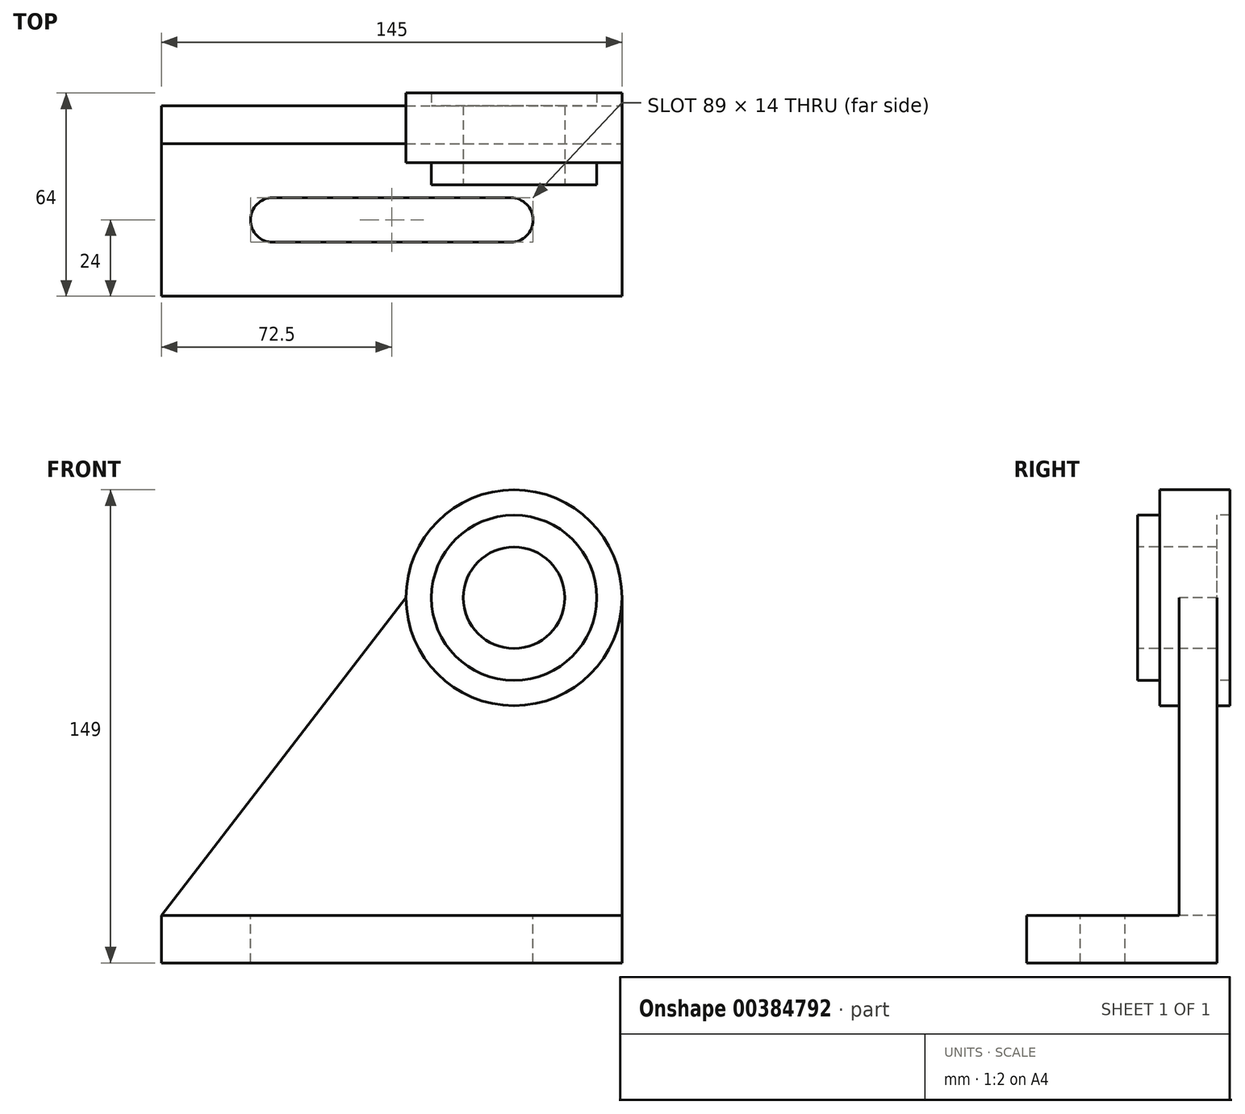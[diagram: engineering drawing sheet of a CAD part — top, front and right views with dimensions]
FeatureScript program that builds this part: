
annotation { "Feature Type Name" : "Feature", "Feature Type Description" : "" }
export const myFeature = defineFeature(function(context is Context, id is Id, definition is map)
    precondition{}
    {
        {
            var Q0;
            Q0=qCreatedBy(makeId("Top.planeOp"),FACE);
            var sketch = newSketch(context, id + "F0", { "sketchPlane" : qUnion([Q0])});
            skLineSegment(sketch, "E0.bottom", {"start": v(-72.5, 30) * mm, "end": v(72.5, 30) * mm});
            skLineSegment(sketch, "E0.top", {"start": v(-72.5, -30) * mm, "end": v(72.5, -30) * mm});
            skLineSegment(sketch, "E0.left", {"start": v(-72.5, 30) * mm, "end": v(-72.5, -30) * mm});
            skLineSegment(sketch, "E0.right", {"start": v(72.5, 30) * mm, "end": v(72.5, -30) * mm});
            skArc(sketch, "E1", {"start": v(-37.5, 1) * mm, "mid": v(-44.5, -6) * mm, "end": v(-37.5, -13) * mm});
            skArc(sketch, "E2", {"start": v(37.5, -13) * mm, "mid": v(44.5, -6) * mm, "end": v(37.5, 1) * mm});
            skLineSegment(sketch, "E3", {"start": v(-37.5, 1) * mm, "end": v(37.5, 1) * mm});
            skLineSegment(sketch, "E4", {"start": v(-37.5, -13) * mm, "end": v(37.5, -13) * mm});
            skSolve(sketch);
        }
        {
            var Q0;
            Q0 = qSketchRegion(id + "F0", true);
            extrude(context, id + "F1", {"entities" : qUnion([Q0]), "oppositeDirection" : true, "depth" : 15 * mm});
        }
        {
            var Q0;
            Q0=qCreatedBy(makeId("Front.planeOp"),FACE);
            var sketch = newSketch(context, id + "F2", { "sketchPlane" : qUnion([Q0])});
            skCircle(sketch, "E5", {"center": v(38.5, 100) * mm, "radius": 16 * mm});
            skCircle(sketch, "E6", {"center": v(38.5, 100) * mm, "radius": 26 * mm});
            skCircle(sketch, "E7", {"center": v(38.5, 100) * mm, "radius": 34 * mm});
            skLineSegment(sketch, "E8", {"start": v(-72.5, -3.66) * mm, "end": v(-72.5, 0) * mm});
            skLineSegment(sketch, "E9", {"start": v(-72.5, 0) * mm, "end": v(-63.73, 0) * mm});
            skLineSegment(sketch, "E10", {"start": v(65, 0) * mm, "end": v(72.5, 0) * mm});
            skLineSegment(sketch, "E11", {"start": v(72.5, 0) * mm, "end": v(72.5, -12.5) * mm});
            skLineSegment(sketch, "E12", {"start": v(72.5, 0) * mm, "end": v(72.5, 100) * mm});
            skLineSegment(sketch, "E13", {"start": v(-63.73, 0) * mm, "end": v(65, 0) * mm});
            skLineSegment(sketch, "E14", {"start": v(-72.5, 0) * mm, "end": v(4.5, 100) * mm});
            skSolve(sketch);
        }
        {
            var Q0;
            Q0=makeQuery(id+"F2.imprint","IMPRINT",FACE,{"disambiguationData":[TD([[makeQuery(id+"F2.imprint","IMPRINT",EDGE,{"derivedFrom":sQuery(id+"F2.wireOp",EDGE,"E9")}),1.0]])]});
            extrude(context, id + "F3", {"entities" : qUnion([Q0]), "operationType" : NewBodyOperationType.ADD, "oppositeDirection" : true, "depth" : 30 * mm, "hasSecondDirection" : true, "secondDirectionOppositeDirection" : true, "secondDirectionDepth" : 18 * mm});
        }
        {
            var Q0;
            Q0=makeQuery(id+"F2.imprint","IMPRINT",FACE,{"disambiguationData":[TD([[makeQuery(id+"F2.imprint","IMPRINT",EDGE,{"derivedFrom":sQuery(id+"F2.wireOp",EDGE,"E6")}),-1.0]])]});
            extrude(context, id + "F4", {"entities" : qUnion([Q0]), "operationType" : NewBodyOperationType.ADD, "oppositeDirection" : true, "depth" : 34 * mm, "hasSecondDirection" : true, "secondDirectionOppositeDirection" : true, "secondDirectionDepth" : 12 * mm});
        }
        {
            var Q0;
            Q0=makeQuery(id+"F2.imprint","IMPRINT",FACE,{"disambiguationData":[TD([[makeQuery(id+"F2.imprint","IMPRINT",EDGE,{"derivedFrom":sQuery(id+"F2.wireOp",EDGE,"E5")}),-1.0]])]});
            extrude(context, id + "F5", {"entities" : qUnion([Q0]), "operationType" : NewBodyOperationType.ADD, "oppositeDirection" : true, "depth" : 30 * mm, "hasSecondDirection" : true, "secondDirectionOppositeDirection" : true, "secondDirectionDepth" : 5 * mm});
        }
    });
